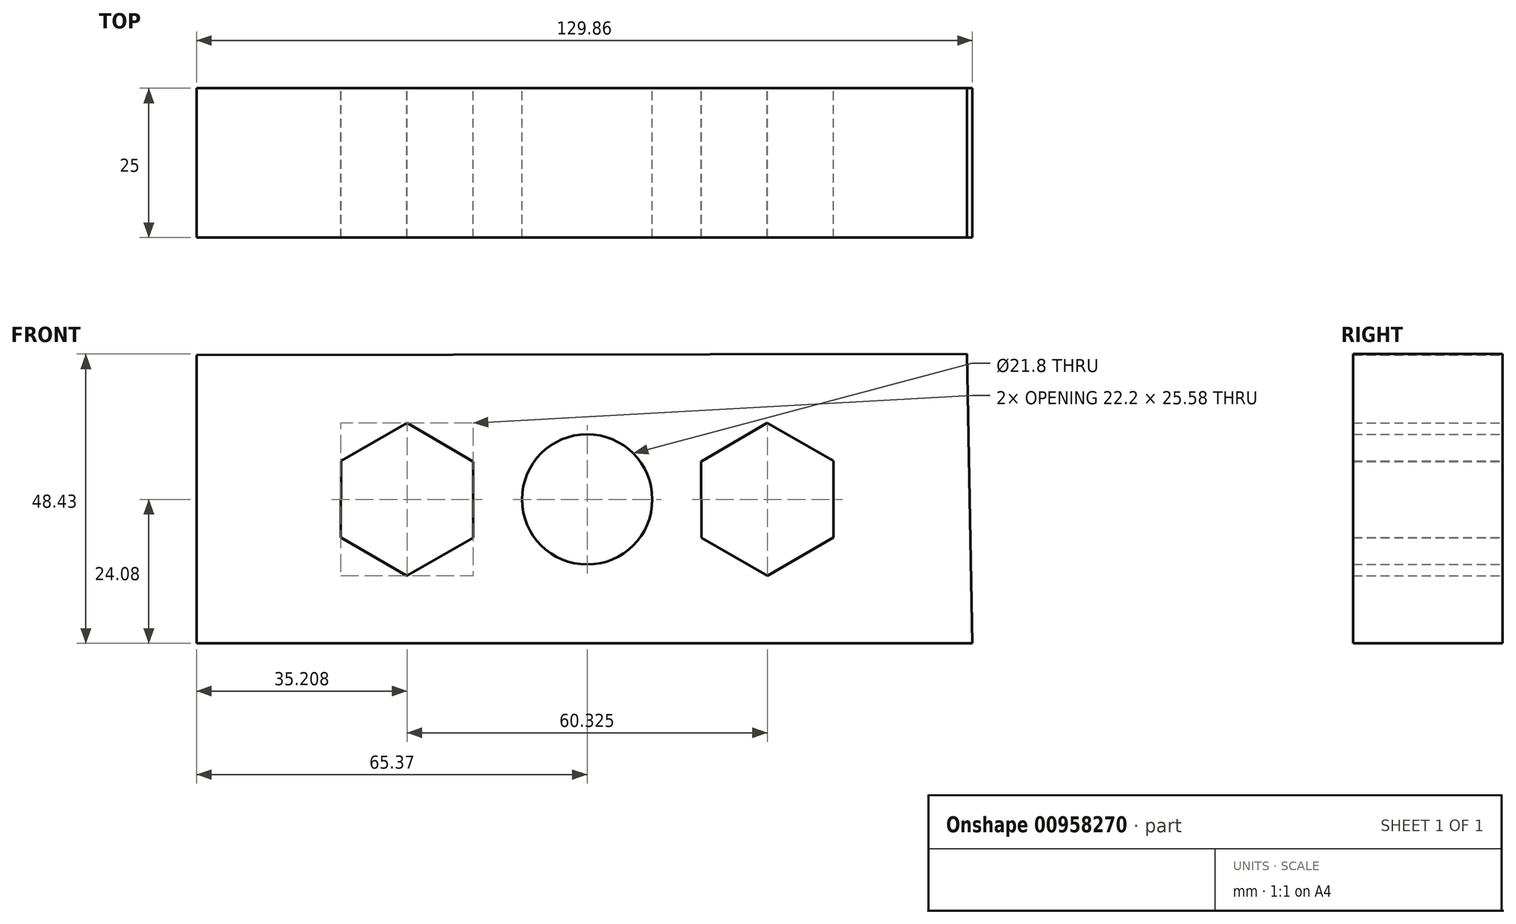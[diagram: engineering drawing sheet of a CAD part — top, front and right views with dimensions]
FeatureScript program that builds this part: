
annotation { "Feature Type Name" : "Feature", "Feature Type Description" : "" }
export const myFeature = defineFeature(function(context is Context, id is Id, definition is map)
    precondition{}
    {
        {
            var Q0;
            Q0=qCreatedBy(makeId("Front.planeOp"),FACE);
            var sketch = newSketch(context, id + "F0", { "sketchPlane" : qUnion([Q0])});
            skLineSegment(sketch, "E0", {"start": v(64.5, -24.08) * mm, "end": v(0, -24.08) * mm});
            skLineSegment(sketch, "E1", {"start": v(0, -24.08) * mm, "end": v(-65.37, -24.08) * mm});
            skLineSegment(sketch, "E2", {"start": v(-65.37, -24.08) * mm, "end": v(-65.37, 24.2) * mm});
            skLineSegment(sketch, "E3", {"start": v(-65.37, 24.2) * mm, "end": v(63.59, 24.35) * mm});
            skLineSegment(sketch, "E4", {"start": v(63.59, 24.35) * mm, "end": v(64.5, -24.08) * mm});
            skCircle(sketch, "E5", {"center": v(0, 0) * mm, "radius": 10.9 * mm});
            skCircle(sketch, "E6.cCircle", {"center": v(-30.16, 0) * mm, "radius": 11.07 * mm, "construction": true});
            skLineSegment(sketch, "E6.0", {"start": v(-30.21, -12.79) * mm, "end": v(-41.26, -6.35) * mm});
            skLineSegment(sketch, "E6.1", {"start": v(-41.26, -6.35) * mm, "end": v(-41.21, 6.44) * mm});
            skLineSegment(sketch, "E6.2", {"start": v(-41.21, 6.44) * mm, "end": v(-30.11, 12.79) * mm});
            skLineSegment(sketch, "E6.3", {"start": v(-30.11, 12.79) * mm, "end": v(-19.06, 6.35) * mm});
            skLineSegment(sketch, "E6.4", {"start": v(-19.06, 6.35) * mm, "end": v(-19.11, -6.44) * mm});
            skLineSegment(sketch, "E6.5", {"start": v(-19.11, -6.44) * mm, "end": v(-30.21, -12.79) * mm});
            skPoint(sketch, "E6.0.midPoint", {"position": v(-35.74, -9.57) * mm});
            skLineSegment(sketch, "E7.MirrorCS", {"start": v(41.26, -6.35) * mm, "end": v(41.21, 6.44) * mm});
            skLineSegment(sketch, "E8.MirrorCS", {"start": v(41.21, 6.44) * mm, "end": v(30.11, 12.79) * mm});
            skLineSegment(sketch, "E9.MirrorCS", {"start": v(30.11, 12.79) * mm, "end": v(19.06, 6.35) * mm});
            skLineSegment(sketch, "E10.MirrorCS", {"start": v(19.06, 6.35) * mm, "end": v(19.11, -6.44) * mm});
            skCircle(sketch, "E11.MirrorC", {"center": v(30.16, 0) * mm, "radius": 11.07 * mm, "construction": true});
            skLineSegment(sketch, "E12.MirrorCS", {"start": v(19.11, -6.44) * mm, "end": v(30.21, -12.79) * mm});
            skLineSegment(sketch, "E13.MirrorCS", {"start": v(30.21, -12.79) * mm, "end": v(41.26, -6.35) * mm});
            skSolve(sketch);
        }
        {
            var Q0;
            Q0=makeQuery(id+"F0.imprint","IMPRINT",FACE,{"disambiguationData":[TD([[makeQuery(id+"F0.imprint","IMPRINT",EDGE,{"derivedFrom":sQuery(id+"F0.wireOp",EDGE,"E0")}),-1.0]])]});
            extrude(context, id + "F1", {"entities" : qUnion([Q0]), "depth" : 25 * mm, "offsetDistance" : 25 * mm});
        }
    });
